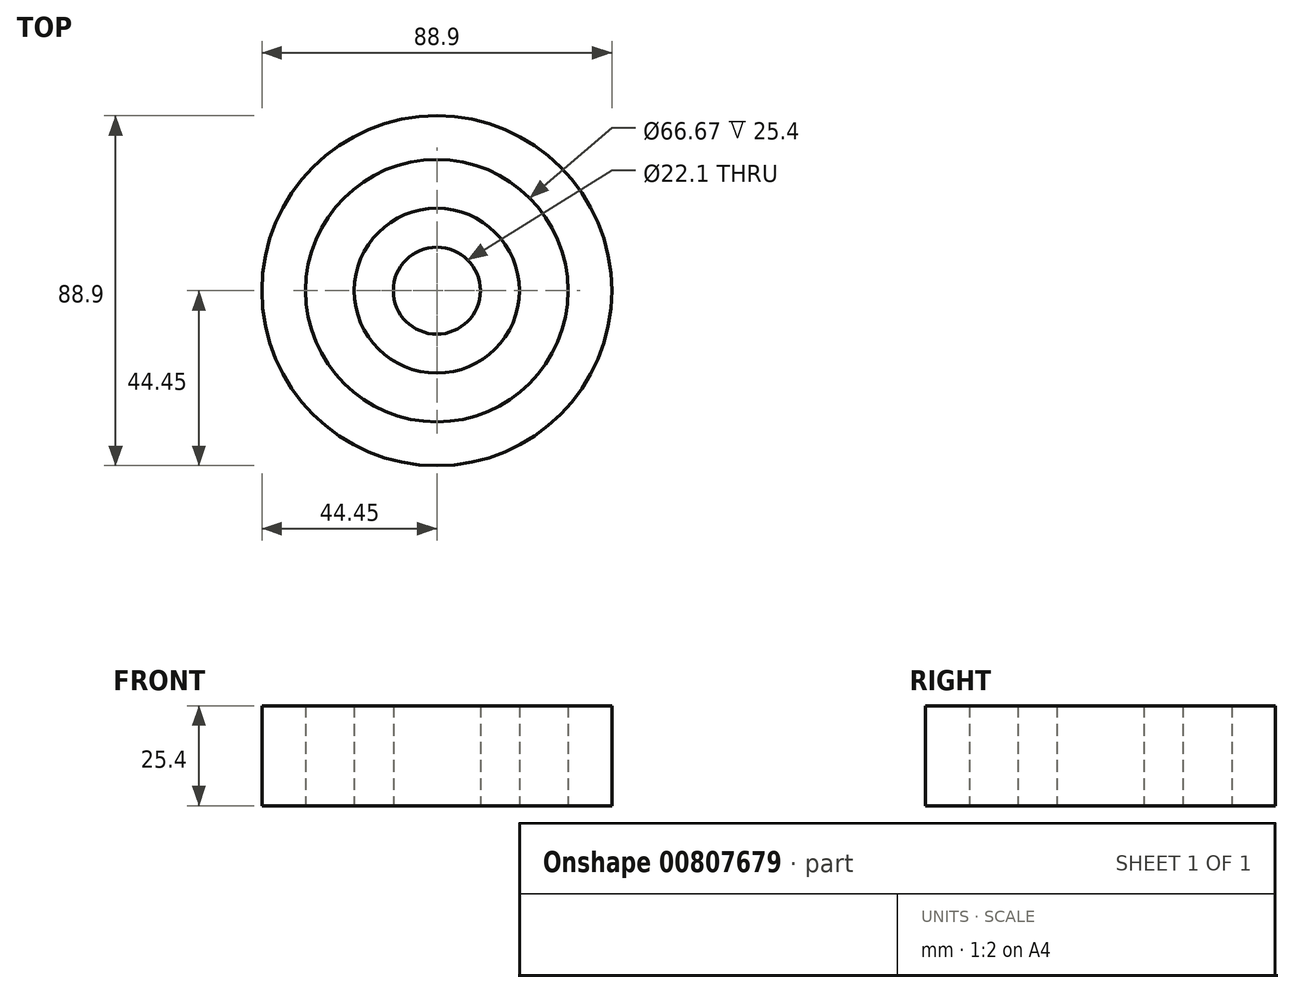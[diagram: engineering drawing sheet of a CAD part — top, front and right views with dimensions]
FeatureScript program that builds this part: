
annotation { "Feature Type Name" : "Feature", "Feature Type Description" : "" }
export const myFeature = defineFeature(function(context is Context, id is Id, definition is map)
    precondition{}
    {
        {
            var Q0;
            Q0=qCreatedBy(makeId("Top.planeOp"),FACE);
            var sketch = newSketch(context, id + "F0", { "sketchPlane" : qUnion([Q0])});
            skCircle(sketch, "E0", {"center": v(0, 0) * mm, "radius": 44.45 * mm});
            skCircle(sketch, "E1", {"center": v(0, 0) * mm, "radius": 11.05 * mm});
            skSolve(sketch);
        }
        {
            var Q0;
            Q0=makeQuery(id+"F0.imprint","IMPRINT",FACE,{"disambiguationData":[TD([[makeQuery(id+"F0.imprint","IMPRINT",EDGE,{"derivedFrom":sQuery(id+"F0.wireOp",EDGE,"E0")}),1.0]])]});
            extrude(context, id + "F1", {"entities" : qUnion([Q0]), "depth" : 25.4 * mm, "offsetDistance" : 25.4 * mm});
        }
        {
            var Q0;
            Q0=makeQuery(id+"F1.opExtrude","CAP_FACE",FACE,{"disambiguationData":[OSD([sQuery(id+"F0.wireOp",EDGE,"E0"),sQuery(id+"F0.wireOp",EDGE,"E1")])],"isStart":false});
            var sketch = newSketch(context, id + "F2", { "sketchPlane" : qUnion([Q0])});
            skLineSegment(sketch, "E2", {"start": v(0, 11.05) * mm, "end": v(0, 44.45) * mm});
            skLineSegment(sketch, "E3", {"start": v(0, 44.45) * mm, "end": v(0, 11.05) * mm});
            skLineSegment(sketch, "E4", {"start": v(0, -11.05) * mm, "end": v(0, -44.45) * mm});
            skPoint(sketch, "E4.startSnap0", {"position": v(0, 27.75) * mm});
            skLineSegment(sketch, "E5", {"start": v(11.05, 0) * mm, "end": v(44.45, 0) * mm});
            skLineSegment(sketch, "E6", {"start": v(-11.05, 0) * mm, "end": v(-44.45, 0) * mm});
            skSolve(sketch);
        }
        {
            var Q0;
            Q0=qCreatedBy(makeId("Top.planeOp"),FACE);
            var sketch = newSketch(context, id + "F3", { "sketchPlane" : qUnion([Q0])});
            skLineSegment(sketch, "E7", {"start": v(0, 0) * mm, "end": v(0, -5.52) * mm, "construction": true});
            skLineSegment(sketch, "E8", {"start": v(0, -5.52) * mm, "end": v(0, -44.5) * mm});
            skLineSegment(sketch, "E9", {"start": v(0, 0) * mm, "end": v(-8.7, -2.76) * mm, "construction": true});
            skPoint(sketch, "E9.endSnap0", {"position": v(0, -2.76) * mm});
            skLineSegment(sketch, "E10", {"start": v(0, 0) * mm, "end": v(-11.4, 0) * mm, "construction": true});
            skLineSegment(sketch, "E11", {"start": v(-5.7, 0) * mm, "end": v(-5.7, -9.44) * mm, "construction": true});
            skCircle(sketch, "E12", {"center": v(0, 0) * mm, "radius": 2.76 * mm, "construction": true});
            skCircle(sketch, "E13", {"center": v(0, 0) * mm, "radius": 44.45 * mm, "construction": true});
            skCircle(sketch, "E14", {"center": v(0, 0) * mm, "radius": 11.11 * mm, "construction": true});
            skCircle(sketch, "E15", {"center": v(0, 0) * mm, "radius": 20.96 * mm});
            skCircle(sketch, "E16", {"center": v(0, 0) * mm, "radius": 33.34 * mm});
            skSolve(sketch);
        }
        {
            var Q0;
            Q0 = qSketchRegion(id + "F3", true);
            var Q1;
            {var subQ0=sQuery(id+"F2.wireOp",EDGE,"E3");Q1=makeQuery(id+"F2.imprint","IMPRINT",FACE,{"disambiguationData":[TD([[makeQuery(id+"F2.imprint","IMPRINT",EDGE,{"derivedFrom":subQ0}),-1.0]])]});}
            extrude(context, id + "F4", {"entities" : qUnion([Q0, Q1]), "operationType" : NewBodyOperationType.REMOVE, "depth" : 25.4 * mm, "offsetDistance" : 25.4 * mm});
        }
    });
